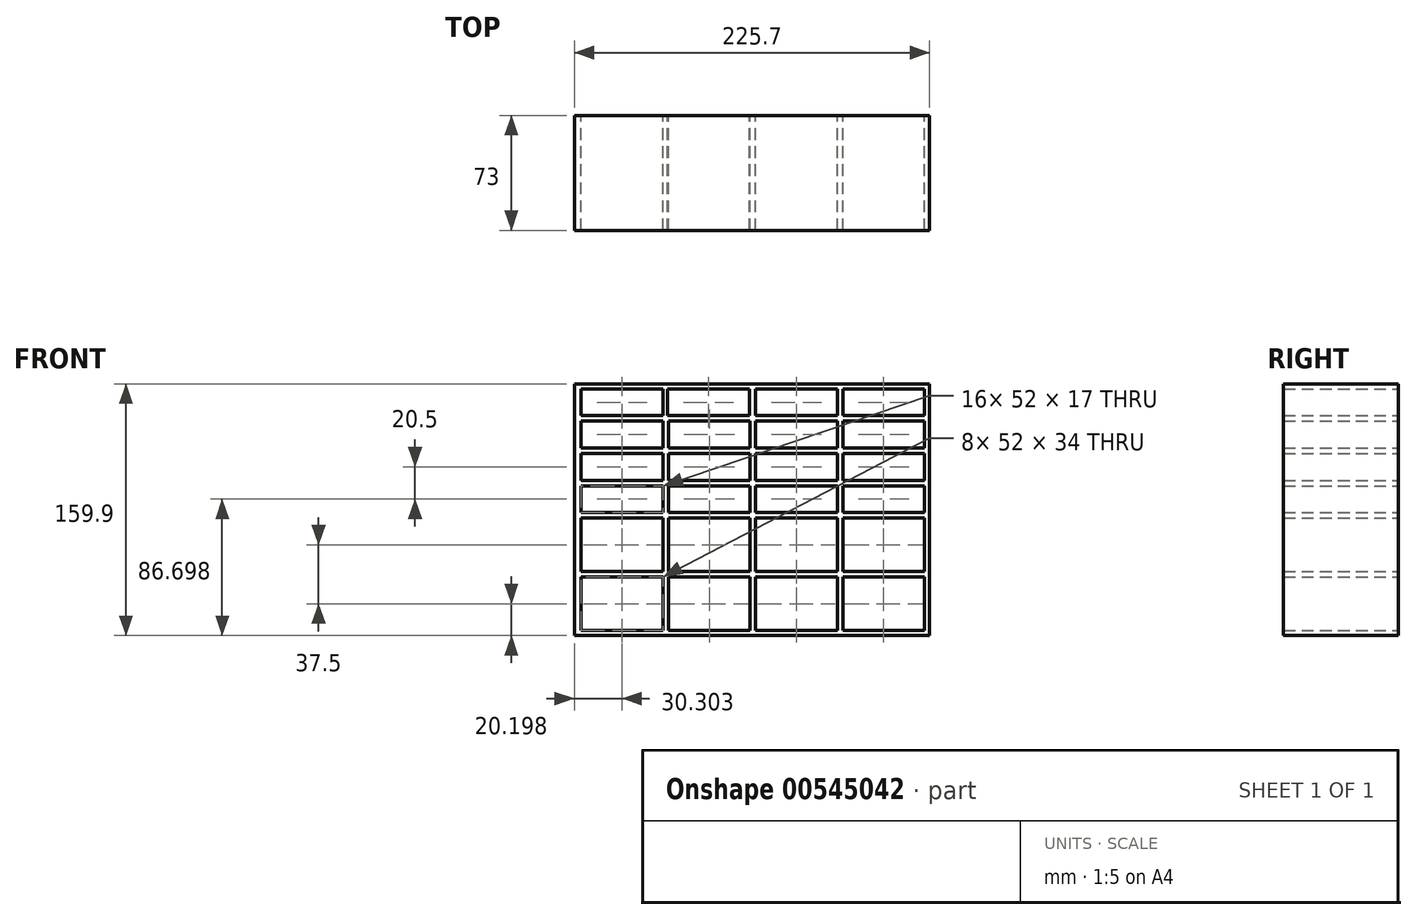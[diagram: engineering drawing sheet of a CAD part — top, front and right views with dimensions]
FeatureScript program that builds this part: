
annotation { "Feature Type Name" : "Feature", "Feature Type Description" : "" }
export const myFeature = defineFeature(function(context is Context, id is Id, definition is map)
    precondition{}
    {
        {
            var Q0;
            Q0=qCreatedBy(makeId("Front.planeOp"),FACE);
            var sketch = newSketch(context, id + "F0", { "sketchPlane" : qUnion([Q0])});
            skLineSegment(sketch, "E0.bottom", {"start": v(-383.44, 42.44) * mm, "end": v(-331.44, 42.44) * mm});
            skLineSegment(sketch, "E0.top", {"start": v(-383.44, 8.44) * mm, "end": v(-331.44, 8.44) * mm});
            skLineSegment(sketch, "E0.left", {"start": v(-383.44, 42.44) * mm, "end": v(-383.44, 8.44) * mm});
            skLineSegment(sketch, "E0.right", {"start": v(-331.44, 42.44) * mm, "end": v(-331.44, 8.44) * mm});
            skLineSegment(sketch, "E1.bottom", {"start": v(-383.44, 45.94) * mm, "end": v(-331.44, 45.94) * mm});
            skLineSegment(sketch, "E1.top", {"start": v(-383.44, 62.94) * mm, "end": v(-331.44, 62.94) * mm});
            skLineSegment(sketch, "E1.left", {"start": v(-383.44, 45.94) * mm, "end": v(-383.44, 62.94) * mm});
            skLineSegment(sketch, "E1.right", {"start": v(-331.44, 45.94) * mm, "end": v(-331.44, 62.94) * mm});
            skLineSegment(sketch, "E2.bottom", {"start": v(-383.44, 66.44) * mm, "end": v(-331.44, 66.44) * mm});
            skLineSegment(sketch, "E2.top", {"start": v(-383.44, 83.44) * mm, "end": v(-331.44, 83.44) * mm});
            skLineSegment(sketch, "E2.left", {"start": v(-383.44, 66.44) * mm, "end": v(-383.44, 83.44) * mm});
            skLineSegment(sketch, "E2.right", {"start": v(-331.44, 66.44) * mm, "end": v(-331.44, 83.44) * mm});
            skLineSegment(sketch, "E3.bottom", {"start": v(-383.44, 86.94) * mm, "end": v(-331.44, 86.94) * mm});
            skLineSegment(sketch, "E3.top", {"start": v(-383.44, 103.94) * mm, "end": v(-331.44, 103.94) * mm});
            skLineSegment(sketch, "E3.left", {"start": v(-383.44, 86.94) * mm, "end": v(-383.44, 103.94) * mm});
            skLineSegment(sketch, "E3.right", {"start": v(-331.44, 86.94) * mm, "end": v(-331.44, 103.94) * mm});
            skLineSegment(sketch, "E4.bottom", {"start": v(-383.44, 4.94) * mm, "end": v(-331.44, 4.94) * mm});
            skLineSegment(sketch, "E4.top", {"start": v(-383.44, -29.06) * mm, "end": v(-331.44, -29.06) * mm});
            skLineSegment(sketch, "E4.left", {"start": v(-383.44, 4.94) * mm, "end": v(-383.44, -29.06) * mm});
            skLineSegment(sketch, "E4.right", {"start": v(-331.44, 4.94) * mm, "end": v(-331.44, -29.06) * mm});
            skLineSegment(sketch, "E5.MirrorCS", {"start": v(-276.04, 45.94) * mm, "end": v(-328.04, 45.94) * mm});
            skLineSegment(sketch, "E6.MirrorCS", {"start": v(-328.04, 66.44) * mm, "end": v(-328.04, 83.44) * mm});
            skLineSegment(sketch, "E7.MirrorCS", {"start": v(-276.04, 83.44) * mm, "end": v(-328.04, 83.44) * mm});
            skLineSegment(sketch, "E8.MirrorCS", {"start": v(-328.5, 107.44) * mm, "end": v(-328.5, 124.44) * mm});
            skLineSegment(sketch, "E9.MirrorCS", {"start": v(-276.04, 103.94) * mm, "end": v(-328.04, 103.94) * mm});
            skLineSegment(sketch, "E10.MirrorCS", {"start": v(-276.04, 86.94) * mm, "end": v(-276.04, 103.94) * mm});
            skLineSegment(sketch, "E11.MirrorCS", {"start": v(-276.04, 66.44) * mm, "end": v(-328.04, 66.44) * mm});
            skLineSegment(sketch, "E12.MirrorCS", {"start": v(-276.04, 42.44) * mm, "end": v(-276.04, 8.44) * mm});
            skLineSegment(sketch, "E13.MirrorCS", {"start": v(-328.04, 42.44) * mm, "end": v(-328.04, 8.44) * mm});
            skLineSegment(sketch, "E14.MirrorCS", {"start": v(-276.04, 66.44) * mm, "end": v(-276.04, 83.44) * mm});
            skLineSegment(sketch, "E15.MirrorCS", {"start": v(-328.04, 45.94) * mm, "end": v(-328.04, 62.94) * mm});
            skLineSegment(sketch, "E16.MirrorCS", {"start": v(-276.04, 8.44) * mm, "end": v(-328.04, 8.44) * mm});
            skLineSegment(sketch, "E17.MirrorCS", {"start": v(-276.04, 62.94) * mm, "end": v(-328.04, 62.94) * mm});
            skLineSegment(sketch, "E18.MirrorCS", {"start": v(-276.5, 124.44) * mm, "end": v(-328.5, 124.44) * mm});
            skLineSegment(sketch, "E19.MirrorCS", {"start": v(-276.04, 45.94) * mm, "end": v(-276.04, 62.94) * mm});
            skLineSegment(sketch, "E20.MirrorCS", {"start": v(-276.04, 86.94) * mm, "end": v(-328.04, 86.94) * mm});
            skLineSegment(sketch, "E21.MirrorCS", {"start": v(-276.04, 4.94) * mm, "end": v(-328.04, 4.94) * mm});
            skLineSegment(sketch, "E22.MirrorCS", {"start": v(-328.04, 86.94) * mm, "end": v(-328.04, 103.94) * mm});
            skLineSegment(sketch, "E23.MirrorCS", {"start": v(-276.04, 42.44) * mm, "end": v(-328.04, 42.44) * mm});
            skLineSegment(sketch, "E24.MirrorCS", {"start": v(-276.5, 107.44) * mm, "end": v(-328.5, 107.44) * mm});
            skLineSegment(sketch, "E25.MirrorCS", {"start": v(-276.5, 107.44) * mm, "end": v(-276.5, 124.44) * mm});
            skLineSegment(sketch, "E26.MirrorCS", {"start": v(-328.04, 4.94) * mm, "end": v(-328.04, -29.06) * mm});
            skLineSegment(sketch, "E27.MirrorCS", {"start": v(-276.04, -29.06) * mm, "end": v(-328.04, -29.06) * mm});
            skLineSegment(sketch, "E28.MirrorCS", {"start": v(-276.04, 4.94) * mm, "end": v(-276.04, -29.06) * mm});
            skLineSegment(sketch, "E29.MirrorCS", {"start": v(-165.24, 66.44) * mm, "end": v(-165.24, 83.44) * mm});
            skLineSegment(sketch, "E30.MirrorCS", {"start": v(-272.64, 4.94) * mm, "end": v(-220.64, 4.94) * mm});
            skLineSegment(sketch, "E31.MirrorCS", {"start": v(-165.24, 86.94) * mm, "end": v(-165.24, 103.94) * mm});
            skLineSegment(sketch, "E32.MirrorCS", {"start": v(-165.24, 107.44) * mm, "end": v(-165.24, 124.44) * mm});
            skLineSegment(sketch, "E33.MirrorCS", {"start": v(-272.64, 8.44) * mm, "end": v(-220.64, 8.44) * mm});
            skLineSegment(sketch, "E34.MirrorCS", {"start": v(-220.64, 45.94) * mm, "end": v(-220.64, 62.94) * mm});
            skLineSegment(sketch, "E35.MirrorCS", {"start": v(-272.64, 4.94) * mm, "end": v(-272.64, -29.06) * mm});
            skLineSegment(sketch, "E36.MirrorCS", {"start": v(-165.24, 45.94) * mm, "end": v(-217.24, 45.94) * mm});
            skLineSegment(sketch, "E37.MirrorCS", {"start": v(-217.24, 4.94) * mm, "end": v(-217.24, -29.06) * mm});
            skLineSegment(sketch, "E38.MirrorCS", {"start": v(-272.64, 45.94) * mm, "end": v(-272.64, 62.94) * mm});
            skLineSegment(sketch, "E39.MirrorCS", {"start": v(-165.24, 62.94) * mm, "end": v(-217.24, 62.94) * mm});
            skLineSegment(sketch, "E40.MirrorCS", {"start": v(-217.24, 107.44) * mm, "end": v(-217.24, 124.44) * mm});
            skLineSegment(sketch, "E41.MirrorCS", {"start": v(-165.24, 83.44) * mm, "end": v(-217.24, 83.44) * mm});
            skLineSegment(sketch, "E42.MirrorCS", {"start": v(-272.64, 86.94) * mm, "end": v(-272.64, 103.94) * mm});
            skLineSegment(sketch, "E43.MirrorCS", {"start": v(-165.24, 86.94) * mm, "end": v(-217.24, 86.94) * mm});
            skLineSegment(sketch, "E44.MirrorCS", {"start": v(-165.24, 66.44) * mm, "end": v(-217.24, 66.44) * mm});
            skLineSegment(sketch, "E45.MirrorCS", {"start": v(-165.24, 107.44) * mm, "end": v(-217.24, 107.44) * mm});
            skLineSegment(sketch, "E46.MirrorCS", {"start": v(-217.24, 45.94) * mm, "end": v(-217.24, 62.94) * mm});
            skLineSegment(sketch, "E47.MirrorCS", {"start": v(-272.64, 62.94) * mm, "end": v(-220.64, 62.94) * mm});
            skLineSegment(sketch, "E48.MirrorCS", {"start": v(-165.24, 124.44) * mm, "end": v(-217.24, 124.44) * mm});
            skLineSegment(sketch, "E49.MirrorCS", {"start": v(-272.64, 45.94) * mm, "end": v(-220.64, 45.94) * mm});
            skLineSegment(sketch, "E50.MirrorCS", {"start": v(-165.24, 45.94) * mm, "end": v(-165.24, 62.94) * mm});
            skLineSegment(sketch, "E51.MirrorCS", {"start": v(-272.64, 66.44) * mm, "end": v(-220.64, 66.44) * mm});
            skLineSegment(sketch, "E52.MirrorCS", {"start": v(-220.64, 42.44) * mm, "end": v(-220.64, 8.44) * mm});
            skLineSegment(sketch, "E53.MirrorCS", {"start": v(-165.24, 8.44) * mm, "end": v(-217.24, 8.44) * mm});
            skLineSegment(sketch, "E54.MirrorCS", {"start": v(-220.64, 86.94) * mm, "end": v(-220.64, 103.94) * mm});
            skLineSegment(sketch, "E55.MirrorCS", {"start": v(-165.24, 4.94) * mm, "end": v(-165.24, -29.06) * mm});
            skLineSegment(sketch, "E56.MirrorCS", {"start": v(-165.24, 42.44) * mm, "end": v(-217.24, 42.44) * mm});
            skLineSegment(sketch, "E57.MirrorCS", {"start": v(-165.24, 4.94) * mm, "end": v(-217.24, 4.94) * mm});
            skLineSegment(sketch, "E58.MirrorCS", {"start": v(-220.64, 66.44) * mm, "end": v(-220.64, 83.44) * mm});
            skLineSegment(sketch, "E59.MirrorCS", {"start": v(-272.64, 107.44) * mm, "end": v(-220.64, 107.44) * mm});
            skLineSegment(sketch, "E60.MirrorCS", {"start": v(-272.64, 66.44) * mm, "end": v(-272.64, 83.44) * mm});
            skLineSegment(sketch, "E61.MirrorCS", {"start": v(-220.64, 107.44) * mm, "end": v(-220.64, 124.44) * mm});
            skLineSegment(sketch, "E62.MirrorCS", {"start": v(-272.64, 107.44) * mm, "end": v(-272.64, 124.44) * mm});
            skLineSegment(sketch, "E63.MirrorCS", {"start": v(-217.24, 86.94) * mm, "end": v(-217.24, 103.94) * mm});
            skLineSegment(sketch, "E64.MirrorCS", {"start": v(-272.64, 42.44) * mm, "end": v(-272.64, 8.44) * mm});
            skLineSegment(sketch, "E65.MirrorCS", {"start": v(-220.64, 4.94) * mm, "end": v(-220.64, -29.06) * mm});
            skLineSegment(sketch, "E66.MirrorCS", {"start": v(-217.24, 42.44) * mm, "end": v(-217.24, 8.44) * mm});
            skLineSegment(sketch, "E67.MirrorCS", {"start": v(-272.64, 103.94) * mm, "end": v(-220.64, 103.94) * mm});
            skLineSegment(sketch, "E68.MirrorCS", {"start": v(-272.64, -29.06) * mm, "end": v(-220.64, -29.06) * mm});
            skLineSegment(sketch, "E69.MirrorCS", {"start": v(-272.64, 42.44) * mm, "end": v(-220.64, 42.44) * mm});
            skLineSegment(sketch, "E70.MirrorCS", {"start": v(-165.24, -29.06) * mm, "end": v(-217.24, -29.06) * mm});
            skLineSegment(sketch, "E71.MirrorCS", {"start": v(-272.64, 83.44) * mm, "end": v(-220.64, 83.44) * mm});
            skLineSegment(sketch, "E72.MirrorCS", {"start": v(-165.24, 42.44) * mm, "end": v(-165.24, 8.44) * mm});
            skLineSegment(sketch, "E73.MirrorCS", {"start": v(-272.64, 124.44) * mm, "end": v(-220.64, 124.44) * mm});
            skLineSegment(sketch, "E74.MirrorCS", {"start": v(-272.64, 86.94) * mm, "end": v(-220.64, 86.94) * mm});
            skLineSegment(sketch, "E75.MirrorCS", {"start": v(-165.24, 103.94) * mm, "end": v(-217.24, 103.94) * mm});
            skLineSegment(sketch, "E76.MirrorCS", {"start": v(-217.24, 66.44) * mm, "end": v(-217.24, 83.44) * mm});
            skLineSegment(sketch, "E77.bottom", {"start": v(-387.74, 127.64) * mm, "end": v(-162.04, 127.64) * mm});
            skLineSegment(sketch, "E77.top", {"start": v(-387.74, -32.26) * mm, "end": v(-162.04, -32.26) * mm});
            skLineSegment(sketch, "E77.left", {"start": v(-387.74, 127.64) * mm, "end": v(-387.74, -32.26) * mm});
            skLineSegment(sketch, "E77.right", {"start": v(-162.04, 127.64) * mm, "end": v(-162.04, -32.26) * mm});
            skLineSegment(sketch, "E78.bottom", {"start": v(-331.44, 107.44) * mm, "end": v(-383.44, 107.44) * mm});
            skLineSegment(sketch, "E78.top", {"start": v(-331.44, 124.44) * mm, "end": v(-383.44, 124.44) * mm});
            skLineSegment(sketch, "E78.left", {"start": v(-331.44, 107.44) * mm, "end": v(-331.44, 124.44) * mm});
            skLineSegment(sketch, "E78.right", {"start": v(-383.44, 107.44) * mm, "end": v(-383.44, 124.44) * mm});
            skSolve(sketch);
        }
        {
            var Q0;
            Q0=makeQuery(id+"F0.imprint","IMPRINT",FACE,{"disambiguationData":[TD([[makeQuery(id+"F0.imprint","IMPRINT",EDGE,{"derivedFrom":sQuery(id+"F0.wireOp",EDGE,"E0.bottom")}),1.0]])]});
            extrude(context, id + "F1", {"entities" : qUnion([Q0]), "depth" : 73 * mm, "offsetDistance" : 25 * mm});
        }
    });
